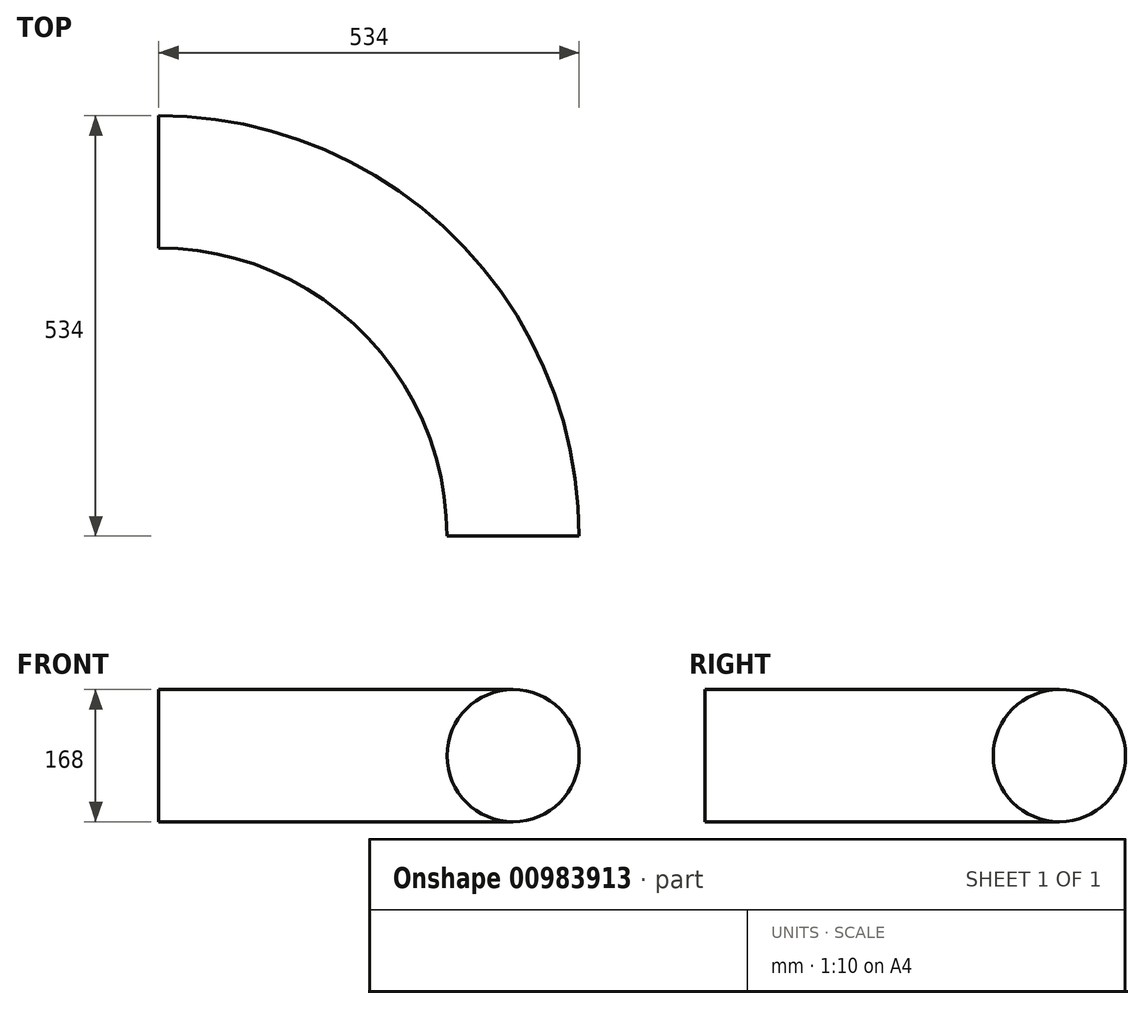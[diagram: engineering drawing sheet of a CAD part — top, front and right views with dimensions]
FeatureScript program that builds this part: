
annotation { "Feature Type Name" : "Feature", "Feature Type Description" : "" }
export const myFeature = defineFeature(function(context is Context, id is Id, definition is map)
    precondition{}
    {
        {
            var Q0;
            Q0=qCreatedBy(makeId("Top.planeOp"),FACE);
            var sketch = newSketch(context, id + "F0", { "sketchPlane" : qUnion([Q0])});
            skArc(sketch, "E0", {"start": v(450, 0) * mm, "mid": v(318.2, 318.2) * mm, "end": v(0, 450) * mm});
            skSolve(sketch);
        }
        {
            var Q0;
            Q0=qCreatedBy(makeId("Front.planeOp"),FACE);
            var sketch = newSketch(context, id + "F1", { "sketchPlane" : qUnion([Q0])});
            skCircle(sketch, "E1", {"center": v(450, 0) * mm, "radius": 84 * mm});
            skSolve(sketch);
        }
        {
            var Q0;
            Q0=makeQuery(id+"F1.imprint","IMPRINT",FACE,{"disambiguationData":[TD([[makeQuery(id+"F1.imprint","IMPRINT",EDGE,{"derivedFrom":sQuery(id+"F1.wireOp",EDGE,"E1")}),1.0]])]});
            var Q1;
            Q1=sQuery(id+"F0.wireOp",EDGE,"E0");
            sweep(context, id + "F2", {"profiles" : qUnion([Q0]), "path" : qUnion([Q1])});
        }
    });
